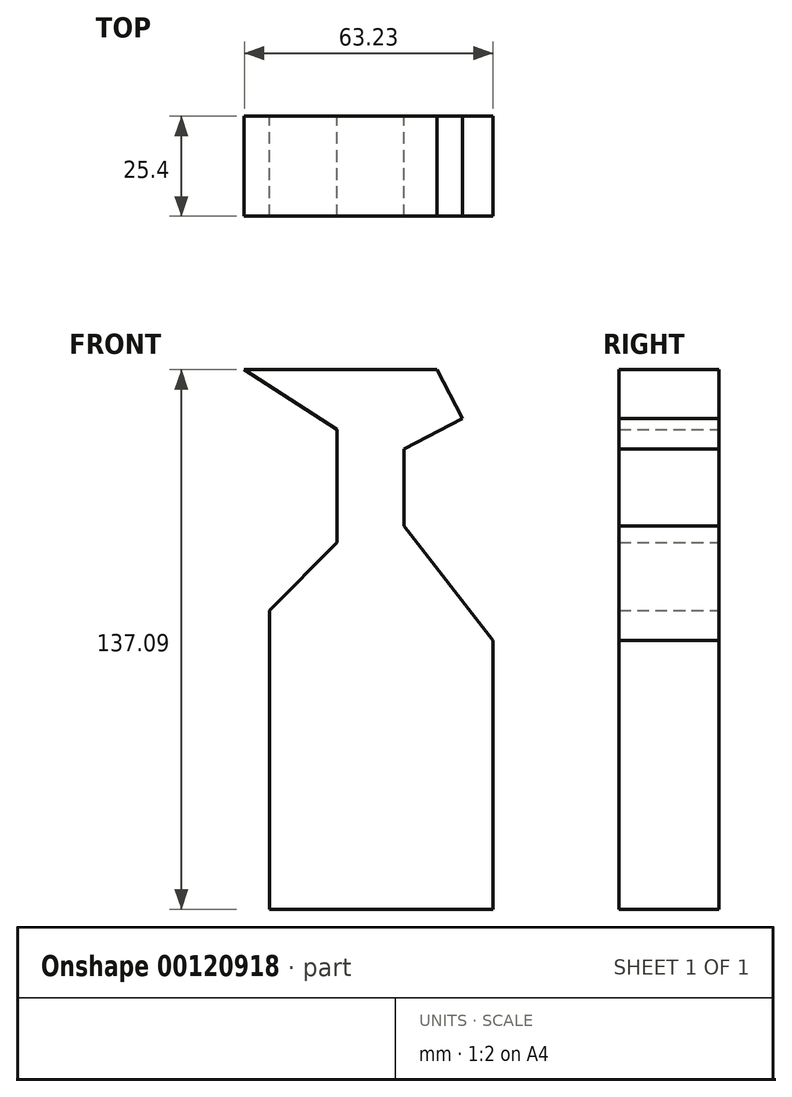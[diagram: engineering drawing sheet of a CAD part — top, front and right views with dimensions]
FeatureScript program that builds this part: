
annotation { "Feature Type Name" : "Feature", "Feature Type Description" : "" }
export const myFeature = defineFeature(function(context is Context, id is Id, definition is map)
    precondition{}
    {
        {
            var Q0;
            Q0=qCreatedBy(makeId("Front.planeOp"),FACE);
            var sketch = newSketch(context, id + "F0", { "sketchPlane" : qUnion([Q0])});
            skLineSegment(sketch, "E0", {"start": v(-30, 61.16) * mm, "end": v(18.93, 61.16) * mm});
            skLineSegment(sketch, "E1", {"start": v(18.93, 61.16) * mm, "end": v(25.39, 48.7) * mm});
            skLineSegment(sketch, "E2", {"start": v(25.39, 48.7) * mm, "end": v(10.55, 41) * mm});
            skLineSegment(sketch, "E3", {"start": v(10.55, 41) * mm, "end": v(10.55, 21.46) * mm});
            skLineSegment(sketch, "E4", {"start": v(10.55, 21.46) * mm, "end": v(33.23, -7.62) * mm});
            skLineSegment(sketch, "E5", {"start": v(33.23, -7.62) * mm, "end": v(33.23, -75.93) * mm});
            skLineSegment(sketch, "E6", {"start": v(33.23, -75.93) * mm, "end": v(-23.54, -75.93) * mm});
            skLineSegment(sketch, "E7", {"start": v(-23.54, -75.93) * mm, "end": v(-23.54, 0) * mm});
            skLineSegment(sketch, "E8", {"start": v(-23.54, 0) * mm, "end": v(-6.46, 17.3) * mm});
            skLineSegment(sketch, "E9", {"start": v(-6.46, 17.3) * mm, "end": v(-6.46, 45.93) * mm});
            skLineSegment(sketch, "E10", {"start": v(-6.46, 45.93) * mm, "end": v(-30, 61.16) * mm});
            skSolve(sketch);
        }
        {
            var Q0;
            Q0 = qSketchRegion(id + "F0", true);
            extrude(context, id + "F1", {"entities" : qUnion([Q0]), "depth" : 25.4 * mm});
        }
    });
